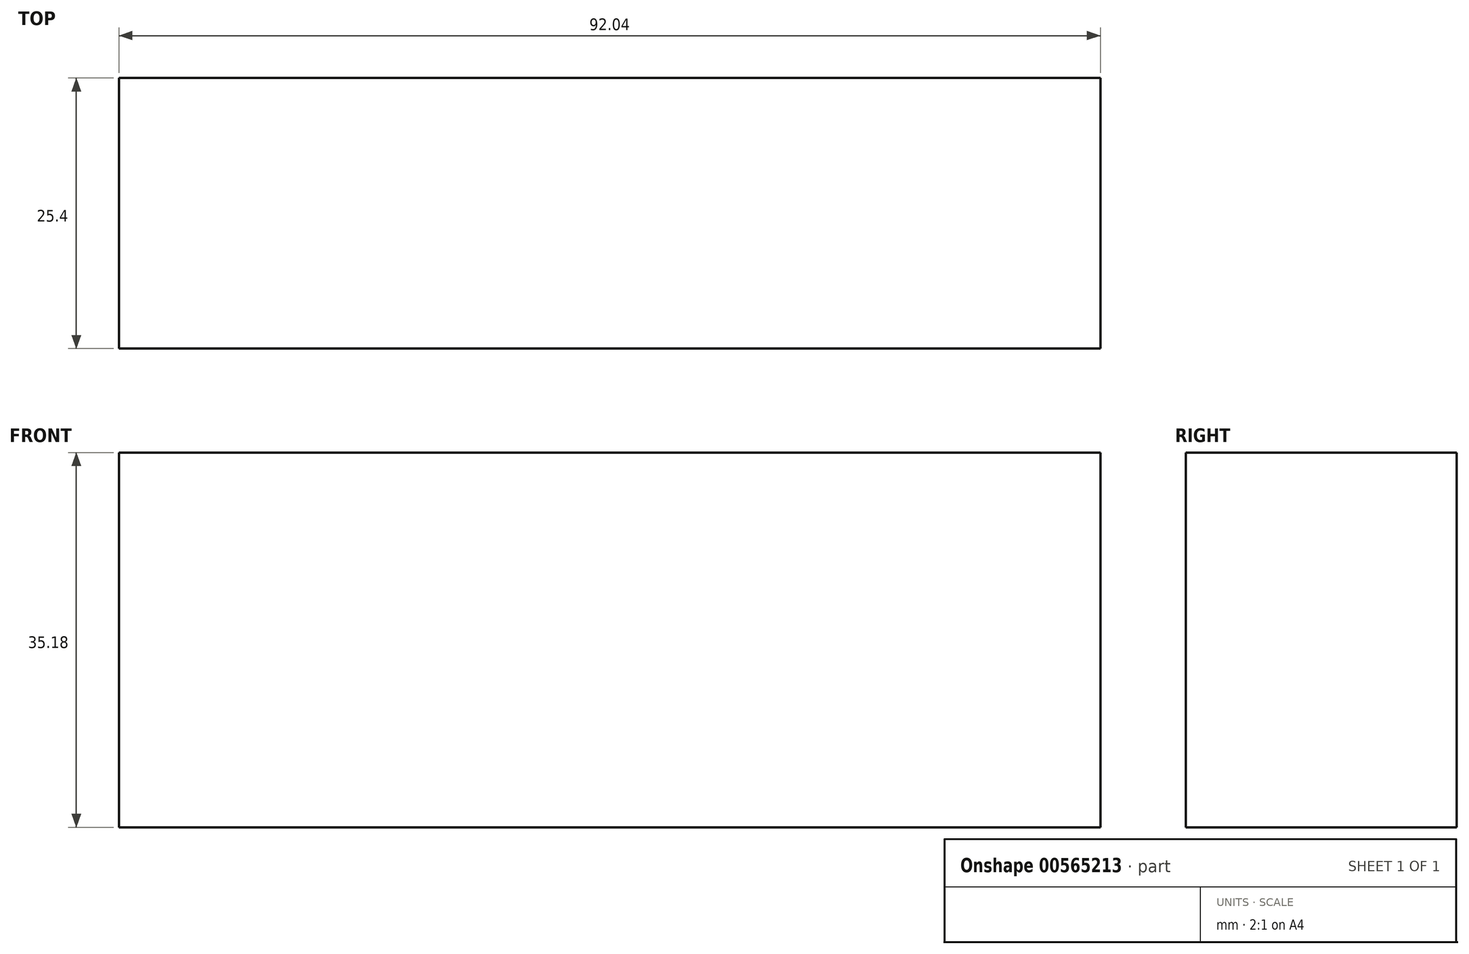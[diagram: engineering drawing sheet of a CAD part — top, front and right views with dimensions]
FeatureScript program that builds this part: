
annotation { "Feature Type Name" : "Feature", "Feature Type Description" : "" }
export const myFeature = defineFeature(function(context is Context, id is Id, definition is map)
    precondition{}
    {
        {
            var Q0;
            Q0=qCreatedBy(makeId("Front.planeOp"),FACE);
            var sketch = newSketch(context, id + "F0", { "sketchPlane" : qUnion([Q0])});
            skLineSegment(sketch, "E0.bottom", {"start": v(-46.02, -17.59) * mm, "end": v(46.02, -17.59) * mm});
            skLineSegment(sketch, "E0.top", {"start": v(-46.02, 17.59) * mm, "end": v(46.02, 17.59) * mm});
            skLineSegment(sketch, "E0.left", {"start": v(-46.02, -17.59) * mm, "end": v(-46.02, 17.59) * mm});
            skLineSegment(sketch, "E0.right", {"start": v(46.02, -17.59) * mm, "end": v(46.02, 17.59) * mm});
            skPoint(sketch, "E0.middle", {"position": v(0, 0) * mm});
            skSolve(sketch);
        }
        {
            var Q0;
            Q0 = qSketchRegion(id + "F0", true);
            extrude(context, id + "F1", {"entities" : qUnion([Q0]), "depth" : 25.4 * mm, "offsetDistance" : 25.4 * mm});
        }
    });
